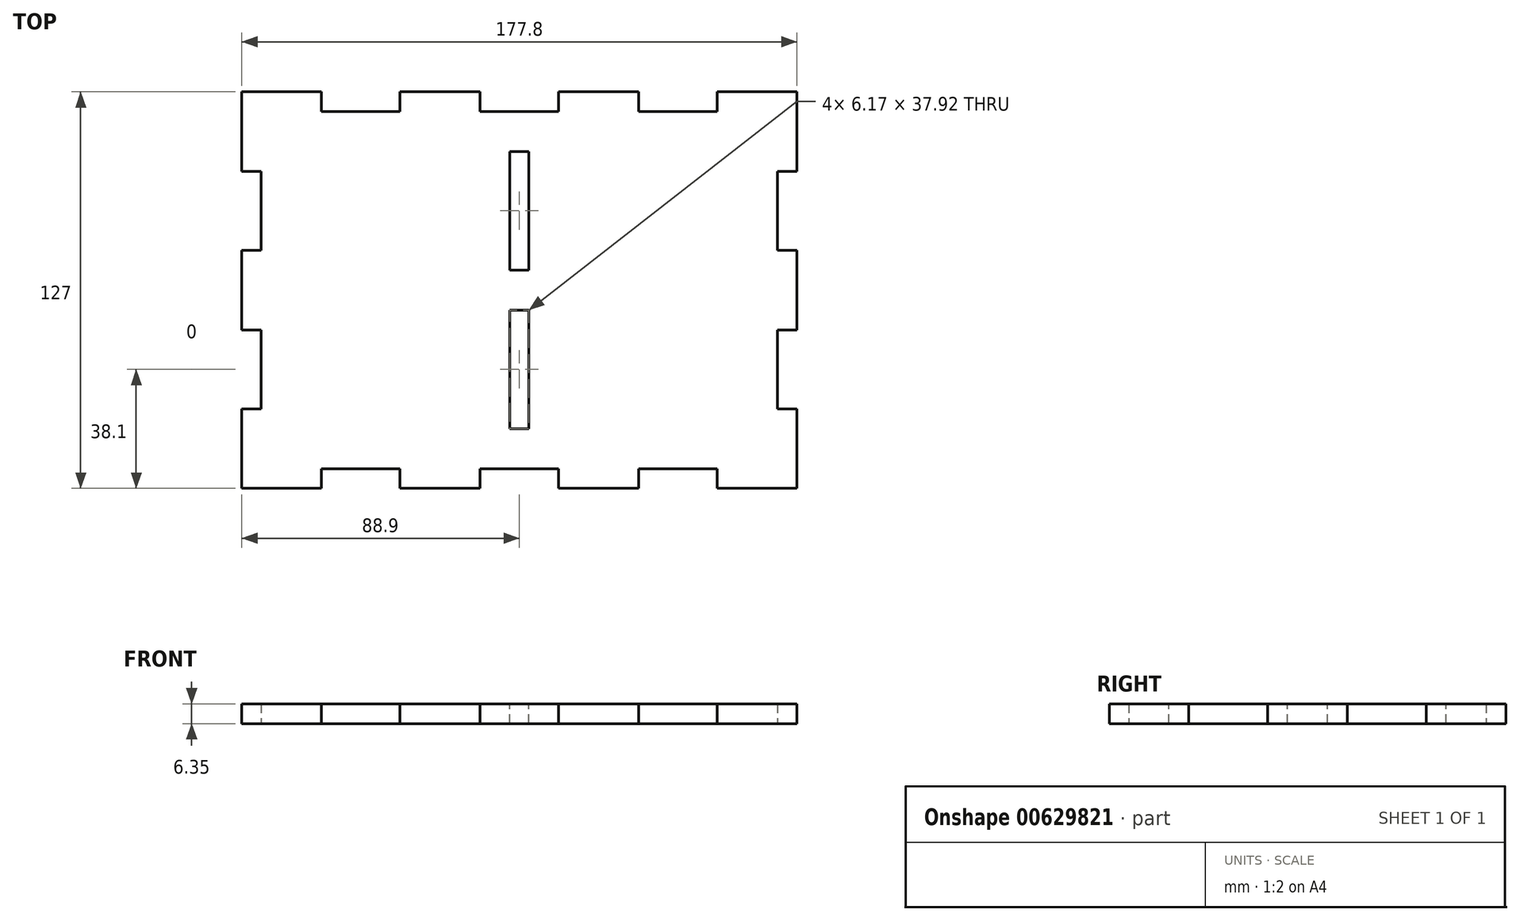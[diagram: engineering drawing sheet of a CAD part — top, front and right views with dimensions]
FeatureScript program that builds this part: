
annotation { "Feature Type Name" : "Feature", "Feature Type Description" : "" }
export const myFeature = defineFeature(function(context is Context, id is Id, definition is map)
    precondition{}
    {
        {
            var Q0;
            Q0=qCreatedBy(makeId("Top.planeOp"),FACE);
            var sketch = newSketch(context, id + "F0", { "sketchPlane" : qUnion([Q0])});
            skLineSegment(sketch, "E0.bottom", {"start": v(0, 0) * mm, "end": v(177.8, 0) * mm});
            skLineSegment(sketch, "E0.top", {"start": v(0, 127) * mm, "end": v(177.8, 127) * mm});
            skLineSegment(sketch, "E0.left", {"start": v(0, 0) * mm, "end": v(0, 127) * mm});
            skLineSegment(sketch, "E0.right", {"start": v(177.8, 0) * mm, "end": v(177.8, 127) * mm});
            skLineSegment(sketch, "E1.bottom", {"start": v(25.49, 0) * mm, "end": v(50.71, 0) * mm});
            skLineSegment(sketch, "E1.top", {"start": v(25.49, 6.26) * mm, "end": v(50.71, 6.26) * mm});
            skLineSegment(sketch, "E1.left", {"start": v(25.49, 0) * mm, "end": v(25.49, 6.26) * mm});
            skLineSegment(sketch, "E1.right", {"start": v(50.71, 0) * mm, "end": v(50.71, 6.26) * mm});
            skPoint(sketch, "E2", {"position": v(38.1, 6.26) * mm});
            skLineSegment(sketch, "E3.1.0.0", {"start": v(76.29, 0) * mm, "end": v(76.29, 6.26) * mm});
            skLineSegment(sketch, "E3.1.0.1", {"start": v(76.29, 6.26) * mm, "end": v(101.51, 6.26) * mm});
            skLineSegment(sketch, "E3.1.0.2", {"start": v(101.51, 0) * mm, "end": v(101.51, 6.26) * mm});
            skPoint(sketch, "E3.1.0.3", {"position": v(88.9, 6.26) * mm});
            skLineSegment(sketch, "E3.2.0.0", {"start": v(127.09, 0) * mm, "end": v(127.09, 6.26) * mm});
            skLineSegment(sketch, "E3.2.0.1", {"start": v(127.09, 6.26) * mm, "end": v(152.31, 6.26) * mm});
            skLineSegment(sketch, "E3.2.0.2", {"start": v(152.31, 0) * mm, "end": v(152.31, 6.26) * mm});
            skPoint(sketch, "E3.2.0.3", {"position": v(139.7, 6.26) * mm});
            skLineSegment(sketch, "E3.direction1", {"start": v(38.1, 6.26) * mm, "end": v(88.9, 6.26) * mm, "construction": true});
            skLineSegment(sketch, "E4.bottom", {"start": v(0, 25.49) * mm, "end": v(6.26, 25.49) * mm});
            skLineSegment(sketch, "E4.top", {"start": v(0, 50.71) * mm, "end": v(6.26, 50.71) * mm});
            skLineSegment(sketch, "E4.left", {"start": v(0, 25.49) * mm, "end": v(0, 50.71) * mm});
            skLineSegment(sketch, "E4.right", {"start": v(6.26, 25.49) * mm, "end": v(6.26, 50.71) * mm});
            skPoint(sketch, "E5", {"position": v(6.26, 38.1) * mm});
            skLineSegment(sketch, "E6.direction1", {"start": v(6.26, 38.1) * mm, "end": v(31.66, 38.1) * mm, "construction": true});
            skLineSegment(sketch, "E7.bottom", {"start": v(25.49, 127) * mm, "end": v(50.71, 127) * mm});
            skLineSegment(sketch, "E7.top", {"start": v(25.49, 120.74) * mm, "end": v(50.71, 120.74) * mm});
            skLineSegment(sketch, "E7.left", {"start": v(25.49, 127) * mm, "end": v(25.49, 120.74) * mm});
            skLineSegment(sketch, "E7.right", {"start": v(50.71, 127) * mm, "end": v(50.71, 120.74) * mm});
            skPoint(sketch, "E8", {"position": v(38.1, 120.74) * mm});
            skLineSegment(sketch, "E9.1.0.0", {"start": v(101.51, 127) * mm, "end": v(101.51, 120.74) * mm});
            skLineSegment(sketch, "E9.1.0.1", {"start": v(76.29, 120.74) * mm, "end": v(101.51, 120.74) * mm});
            skLineSegment(sketch, "E9.1.0.2", {"start": v(76.29, 127) * mm, "end": v(76.29, 120.74) * mm});
            skPoint(sketch, "E9.1.0.3", {"position": v(88.9, 120.74) * mm});
            skLineSegment(sketch, "E9.2.0.0", {"start": v(152.31, 127) * mm, "end": v(152.31, 120.74) * mm});
            skLineSegment(sketch, "E9.2.0.1", {"start": v(127.09, 120.74) * mm, "end": v(152.31, 120.74) * mm});
            skLineSegment(sketch, "E9.2.0.2", {"start": v(127.09, 127) * mm, "end": v(127.09, 120.74) * mm});
            skPoint(sketch, "E9.2.0.3", {"position": v(139.7, 120.74) * mm});
            skLineSegment(sketch, "E9.direction1", {"start": v(38.1, 120.74) * mm, "end": v(88.9, 120.74) * mm, "construction": true});
            skLineSegment(sketch, "E10.0.1.0", {"start": v(0, 101.51) * mm, "end": v(6.26, 101.51) * mm});
            skLineSegment(sketch, "E10.0.1.1", {"start": v(6.26, 76.29) * mm, "end": v(6.26, 101.51) * mm});
            skLineSegment(sketch, "E10.0.1.2", {"start": v(0, 76.29) * mm, "end": v(6.26, 76.29) * mm});
            skPoint(sketch, "E10.0.1.3", {"position": v(6.26, 88.9) * mm});
            skLineSegment(sketch, "E10.direction2", {"start": v(6.26, 38.1) * mm, "end": v(6.26, 88.9) * mm, "construction": true});
            skLineSegment(sketch, "E11", {"start": v(88.9, 127) * mm, "end": v(88.9, 0) * mm, "construction": true});
            skLineSegment(sketch, "E12.MirrorCS", {"start": v(177.8, 101.51) * mm, "end": v(171.54, 101.51) * mm});
            skLineSegment(sketch, "E13.MirrorCS", {"start": v(171.54, 76.29) * mm, "end": v(171.54, 101.51) * mm});
            skLineSegment(sketch, "E14.MirrorCS", {"start": v(177.8, 76.29) * mm, "end": v(171.54, 76.29) * mm});
            skLineSegment(sketch, "E15.MirrorCS", {"start": v(177.8, 50.71) * mm, "end": v(171.54, 50.71) * mm});
            skLineSegment(sketch, "E16.MirrorCS", {"start": v(171.54, 38.1) * mm, "end": v(171.54, 88.9) * mm, "construction": true});
            skLineSegment(sketch, "E17.MirrorCS", {"start": v(171.54, 25.49) * mm, "end": v(171.54, 50.71) * mm});
            skLineSegment(sketch, "E18.MirrorCS", {"start": v(177.8, 25.49) * mm, "end": v(171.54, 25.49) * mm});
            skSolve(sketch);
        }
        {
            var Q0;
            Q0=makeQuery(id+"F0.imprint","IMPRINT",FACE,{"disambiguationData":[TD([[makeQuery(id+"F0.imprint","IMPRINT",EDGE,{"derivedFrom":sQuery(id+"F0.wireOp",EDGE,"E1.top")}),1.0]])]});
            extrude(context, id + "F1", {"entities" : qUnion([Q0]), "depth" : 6.35 * mm, "offsetDistance" : 25.4 * mm});
        }
        {
            var Q0;
            Q0=makeQuery(id+"F1.opExtrude","CAP_FACE",FACE,{"disambiguationData":[OSD([sQuery(id+"F0.wireOp",EDGE,"E0.bottom"),sQuery(id+"F0.wireOp",EDGE,"E0.top"),sQuery(id+"F0.wireOp",EDGE,"E0.left"),sQuery(id+"F0.wireOp",EDGE,"E0.right"),sQuery(id+"F0.wireOp",EDGE,"E1.top"),sQuery(id+"F0.wireOp",EDGE,"E1.left"),sQuery(id+"F0.wireOp",EDGE,"E1.right"),sQuery(id+"F0.wireOp",EDGE,"E3.1.0.0"),sQuery(id+"F0.wireOp",EDGE,"E3.1.0.1"),sQuery(id+"F0.wireOp",EDGE,"E3.1.0.2"),sQuery(id+"F0.wireOp",EDGE,"E3.2.0.0"),sQuery(id+"F0.wireOp",EDGE,"E3.2.0.1"),sQuery(id+"F0.wireOp",EDGE,"E3.2.0.2"),sQuery(id+"F0.wireOp",EDGE,"E4.bottom"),sQuery(id+"F0.wireOp",EDGE,"E4.top"),sQuery(id+"F0.wireOp",EDGE,"E4.right"),sQuery(id+"F0.wireOp",EDGE,"E7.top"),sQuery(id+"F0.wireOp",EDGE,"E7.left"),sQuery(id+"F0.wireOp",EDGE,"E7.right"),sQuery(id+"F0.wireOp",EDGE,"E9.1.0.0"),sQuery(id+"F0.wireOp",EDGE,"E9.1.0.1"),sQuery(id+"F0.wireOp",EDGE,"E9.1.0.2"),sQuery(id+"F0.wireOp",EDGE,"E9.2.0.0"),sQuery(id+"F0.wireOp",EDGE,"E9.2.0.1"),sQuery(id+"F0.wireOp",EDGE,"E9.2.0.2"),sQuery(id+"F0.wireOp",EDGE,"E10.0.1.0"),sQuery(id+"F0.wireOp",EDGE,"E10.0.1.1"),sQuery(id+"F0.wireOp",EDGE,"E10.0.1.2"),sQuery(id+"F0.wireOp",EDGE,"E12.MirrorCS"),sQuery(id+"F0.wireOp",EDGE,"E13.MirrorCS"),sQuery(id+"F0.wireOp",EDGE,"E14.MirrorCS"),sQuery(id+"F0.wireOp",EDGE,"E15.MirrorCS"),sQuery(id+"F0.wireOp",EDGE,"E17.MirrorCS"),sQuery(id+"F0.wireOp",EDGE,"E18.MirrorCS")])],"isStart":false});
            var sketch = newSketch(context, id + "F2", { "sketchPlane" : qUnion([Q0])});
            skLineSegment(sketch, "E19.bottom", {"start": v(85.81, 107.86) * mm, "end": v(91.99, 107.86) * mm});
            skLineSegment(sketch, "E19.top", {"start": v(85.81, 69.94) * mm, "end": v(91.99, 69.94) * mm});
            skLineSegment(sketch, "E19.left", {"start": v(85.81, 107.86) * mm, "end": v(85.81, 69.94) * mm});
            skLineSegment(sketch, "E19.right", {"start": v(91.99, 107.86) * mm, "end": v(91.99, 69.94) * mm});
            skLineSegment(sketch, "E20.bottom", {"start": v(85.81, 57.06) * mm, "end": v(91.99, 57.06) * mm});
            skLineSegment(sketch, "E20.top", {"start": v(85.81, 19.14) * mm, "end": v(91.99, 19.14) * mm});
            skLineSegment(sketch, "E20.left", {"start": v(85.81, 57.06) * mm, "end": v(85.81, 19.14) * mm});
            skLineSegment(sketch, "E20.right", {"start": v(91.99, 57.06) * mm, "end": v(91.99, 19.14) * mm});
            skPoint(sketch, "E21.firstSnap0", {"position": v(88.9, 57.06) * mm});
            skPoint(sketch, "E22", {"position": v(88.9, 19.14) * mm});
            skPoint(sketch, "E23", {"position": v(88.9, 6.26) * mm});
            skPoint(sketch, "E24", {"position": v(88.9, 69.94) * mm});
            skPoint(sketch, "E25", {"position": v(91.99, 38.1) * mm});
            skPoint(sketch, "E26", {"position": v(91.99, 88.9) * mm});
            skSolve(sketch);
        }
        {
            var Q0;
            Q0=makeQuery(id+"F2.imprint","IMPRINT",FACE,{"disambiguationData":[TD([[makeQuery(id+"F2.imprint","IMPRINT",EDGE,{"derivedFrom":sQuery(id+"F2.wireOp",EDGE,"E20.bottom")}),-1.0]])]});
            var Q1;
            Q1=makeQuery(id+"F2.imprint","IMPRINT",FACE,{"disambiguationData":[TD([[makeQuery(id+"F2.imprint","IMPRINT",EDGE,{"derivedFrom":sQuery(id+"F2.wireOp",EDGE,"E19.bottom")}),-1.0]])]});
            extrude(context, id + "F3", {"entities" : qUnion([Q0, Q1]), "operationType" : NewBodyOperationType.REMOVE, "endBound" : BoundingType.THROUGH_ALL, "oppositeDirection" : true, "depth" : 254 * mm, "offsetDistance" : 25.4 * mm});
        }
    });
